# Revit family: Symbotic - Bot Rail
name_source: partatom
category: Structural Framing
revit_build: Autodesk Revit 2017 (Build: 20160720_1515(x64)
units: mm (PartAtom-declared; Revit-internal decimal feet)

## family parameters
Always export as geometry = No
Always vertical = No
Cut with Voids When Loaded = No
Material for Model Behavior = Other
Section Shape = Not Defined
Shared = No
Show family pre-cut in plan views = Yes
Structural Framing Length Roundoff = 0' - 0"
Work Plane-Based = Yes

## types (7) — shared parameters
Default Elevation = 0' - 0"

## per-type parameters (varying)
| type | Beam Length | Show 195-00091 | Show 195-00185 | Show 195-00193 | Show 195-00795A | Show 195-00827 | Show 195-00828 |
| 195-00091 | 26' - 7 13/32" | Yes | No | No | No | No | No |
| 195-00827 | 26' - 10 11/16" | No | No | No | No | Yes | No |
| 195-00185 | 11' - 8 29/32" | No | Yes | No | No | No | No |
| 195-00193 | 17' - 8 29/32" | No | No | Yes | No | No | No |
| 195-00795 | 18' - 1 1/4" | No | No | No | No | No | No |
| 195-00795A | 18' - 1 1/4" | No | No | No | Yes | No | No |
| 195-00828 | 26' - 10 11/16" | No | No | No | No | No | Yes |
